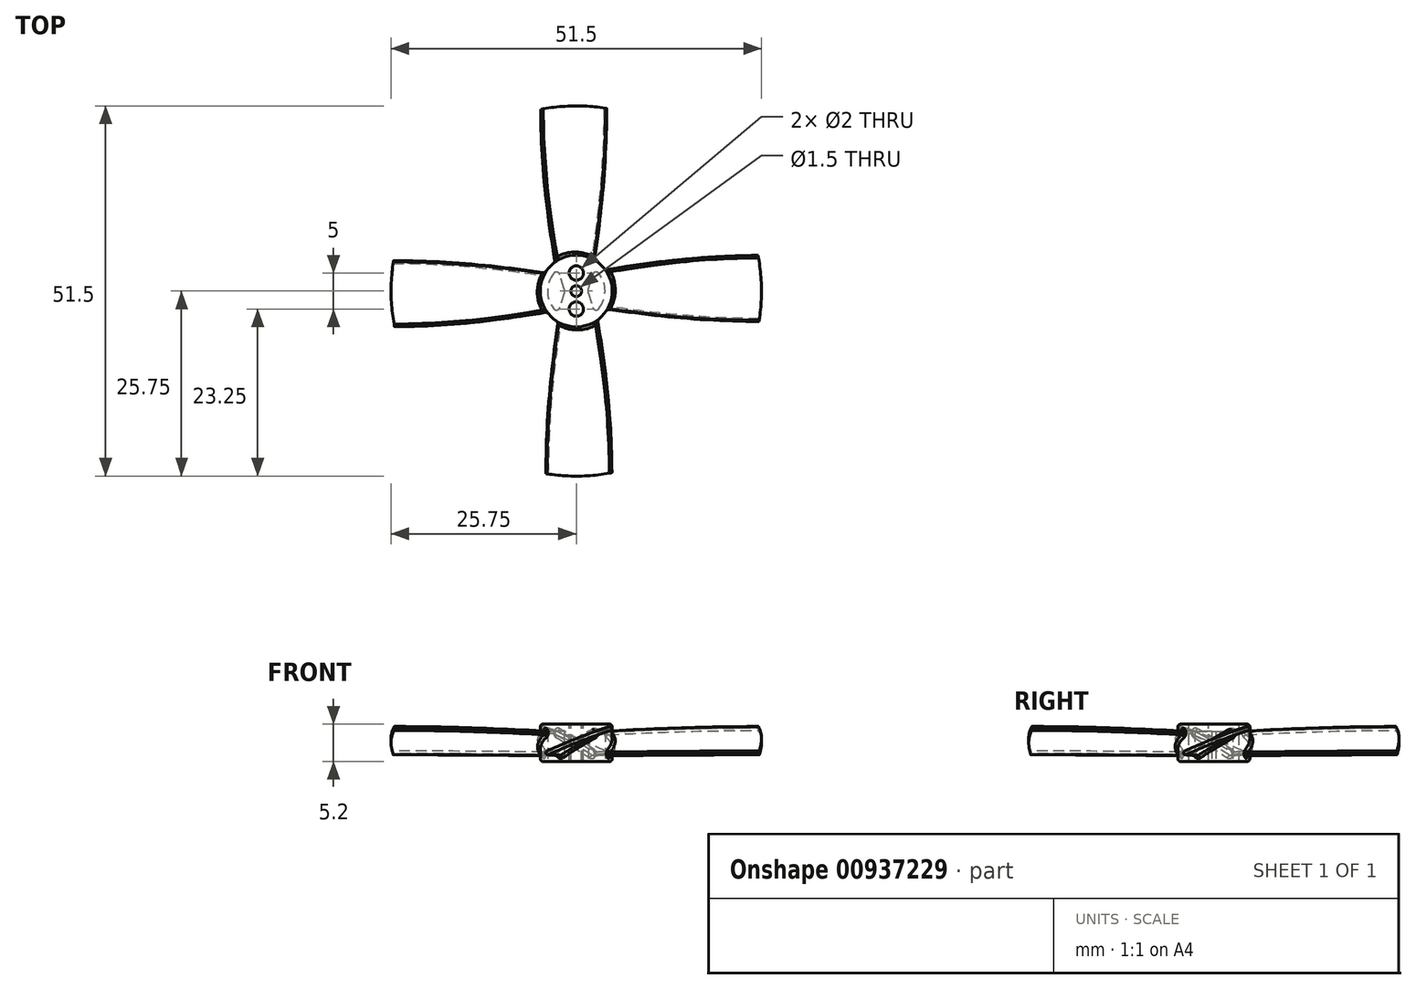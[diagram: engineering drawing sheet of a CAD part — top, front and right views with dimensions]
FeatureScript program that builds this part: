
annotation { "Feature Type Name" : "Feature", "Feature Type Description" : "" }
export const myFeature = defineFeature(function(context is Context, id is Id, definition is map)
    precondition{}
    {
        {
            var Q0;
            Q0=qCreatedBy(makeId("Top.planeOp"),FACE);
            var sketch = newSketch(context, id + "F0", { "sketchPlane" : qUnion([Q0])});
            skCircle(sketch, "E0", {"center": v(0, 0) * mm, "radius": 5 * mm});
            skPoint(sketch, "E1", {"position": v(0, 2.5) * mm});
            skPoint(sketch, "E2.MirrorP", {"position": v(0, -2.5) * mm});
            skSolve(sketch);
        }
        {
            var Q0;
            Q0=makeQuery(id+"F0.imprint","IMPRINT",FACE,{"disambiguationData":[TD([[makeQuery(id+"F0.imprint","IMPRINT",EDGE,{"derivedFrom":sQuery(id+"F0.wireOp",EDGE,"E0")}),1.0]])]});
            extrude(context, id + "F1", {"entities" : qUnion([Q0]), "oppositeDirection" : true, "depth" : 5.2 * mm, "offsetDistance" : 25 * mm});
        }
        {
            var Q0;
            Q0=qCreatedBy(makeId("Front.planeOp"),FACE);
            cPlane(context, id + "F2", {"entities" : qUnion([Q0]), "cplaneType" : CPlaneType.OFFSET, "offset" : (51.5 / 2) * mm, "width" : 150 * mm, "height" : 150 * mm});
        }
        {
            var Q0;
            Q0=qCreatedBy(id+"F2.planeOp",FACE);
            var sketch = newSketch(context, id + "F3", { "sketchPlane" : qUnion([Q0])});
            skArc(sketch, "E3", {"start": v(4.85, -0.26) * mm, "mid": v(0.22, -1.92) * mm, "end": v(-4.31, -3.85) * mm});
            skArc(sketch, "E4.0", {"start": v(5.02, -0.79) * mm, "mid": v(0.42, -2.43) * mm, "end": v(-4.08, -4.35) * mm});
            skLineSegment(sketch, "E5", {"start": v(30.5, -79.2) * mm, "end": v(-4.31, -3.85) * mm});
            skLineSegment(sketch, "E6", {"start": v(30.5, -79.2) * mm, "end": v(4.85, -0.26) * mm});
            skSolve(sketch);
        }
        {
            var Q0;
            Q0=qCreatedBy(makeId("Front.planeOp"),FACE);
            var sketch = newSketch(context, id + "F4", { "sketchPlane" : qUnion([Q0])});
            skArc(sketch, "E7", {"start": v(2.06, -1.11) * mm, "mid": v(0, -2.58) * mm, "end": v(-2.01, -4.11) * mm});
            skArc(sketch, "E8.0", {"start": v(2.37, -1.56) * mm, "mid": v(0.33, -3.02) * mm, "end": v(-1.67, -4.54) * mm});
            skLineSegment(sketch, "E9", {"start": v(48.93, -69) * mm, "end": v(-2.01, -4.11) * mm});
            skLineSegment(sketch, "E10", {"start": v(48.93, -69) * mm, "end": v(2.06, -1.11) * mm});
            skPoint(sketch, "E11", {"position": v(0, -2.58) * mm});
            skSolve(sketch);
        }
        {
            var Q0;
            {var subQ0=sQuery(id+"F4.wireOp",EDGE,"E7");Q0=makeQuery(id+"F4.imprint","IMPRINT",FACE,{"disambiguationData":[TD([[makeQuery(id+"F4.imprint","IMPRINT",EDGE,{"derivedFrom":subQ0}),1.0]])]});}
            var Q1;
            {var subQ0=sQuery(id+"F3.wireOp",EDGE,"E3");Q1=makeQuery(id+"F3.imprint","IMPRINT",FACE,{"disambiguationData":[TD([[makeQuery(id+"F3.imprint","IMPRINT",EDGE,{"derivedFrom":subQ0}),1.0]])]});}
            loft(context, id + "F5", {"startCondition" : LoftEndDerivativeType.TANGENT_TO_PROFILE, "startMagnitude" : 0, "endCondition" : LoftEndDerivativeType.NORMAL_TO_PROFILE, "endMagnitude" : 1.2, "sheetProfilesArray" : [{ "sheetProfileEntities" : qUnion([Q0]) }, { "sheetProfileEntities" : qUnion([Q1]) }]});
        }
        {
            var Q0;
            Q0=makeQuery(id+"F5.opLoft","SWEPT_EDGE",EDGE,{"disambiguationData":[OSD([sQuery(id+"F3.wireOp",EDGE,"E3"),sQuery(id+"F3.wireOp",EDGE,"E6"),sQuery(id+"F4.wireOp",EDGE,"E7"),sQuery(id+"F4.wireOp",EDGE,"E10")])]});
            var Q1;
            Q1=makeQuery(id+"F5.opLoft","SWEPT_EDGE",EDGE,{"disambiguationData":[OSD([sQuery(id+"F3.wireOp",EDGE,"E4.0"),sQuery(id+"F3.wireOp",EDGE,"E6"),sQuery(id+"F4.wireOp",EDGE,"E8.0"),sQuery(id+"F4.wireOp",EDGE,"E10")])]});
            var Q2;
            Q2=makeQuery(id+"F5.opLoft","SWEPT_EDGE",EDGE,{"disambiguationData":[OSD([sQuery(id+"F3.wireOp",EDGE,"E3"),sQuery(id+"F3.wireOp",EDGE,"E5"),sQuery(id+"F4.wireOp",EDGE,"E7"),sQuery(id+"F4.wireOp",EDGE,"E9")])]});
            var Q3;
            Q3=makeQuery(id+"F5.opLoft","SWEPT_EDGE",EDGE,{"disambiguationData":[OSD([sQuery(id+"F3.wireOp",EDGE,"E4.0"),sQuery(id+"F3.wireOp",EDGE,"E5"),sQuery(id+"F4.wireOp",EDGE,"E8.0"),sQuery(id+"F4.wireOp",EDGE,"E9")])]});
            fillet(context, id + "F6", {"entities" : qUnion([Q0, Q1, Q2, Q3]), "radius" : 0.27 * mm, "tangentPropagation" : true, "allowEdgeOverflow" : false});
        }
        {
            var Q0;
            Q0=qCreatedBy(makeId("Top.planeOp"),FACE);
            var sketch = newSketch(context, id + "F7", { "sketchPlane" : qUnion([Q0])});
            skCircle(sketch, "E12", {"center": v(0, 0) * mm, "radius": 25.75 * mm});
            skLineSegment(sketch, "E13.bottom", {"start": v(-26.5, 26.5) * mm, "end": v(26.5, 26.5) * mm});
            skLineSegment(sketch, "E13.top", {"start": v(-26.5, -26.5) * mm, "end": v(26.5, -26.5) * mm});
            skLineSegment(sketch, "E13.left", {"start": v(-26.5, 26.5) * mm, "end": v(-26.5, -26.5) * mm});
            skLineSegment(sketch, "E13.right", {"start": v(26.5, 26.5) * mm, "end": v(26.5, -26.5) * mm});
            skSolve(sketch);
        }
        {
            var Q0;
            Q0=makeQuery(id+"F7.imprint","IMPRINT",FACE,{"disambiguationData":[TD([[makeQuery(id+"F7.imprint","IMPRINT",EDGE,{"derivedFrom":sQuery(id+"F7.wireOp",EDGE,"E12")}),-1.0]])]});
            extrude(context, id + "F8", {"entities" : qUnion([Q0]), "operationType" : NewBodyOperationType.REMOVE, "oppositeDirection" : true, "depth" : 25 * mm, "offsetDistance" : 25 * mm});
        }
        {
            var Q0;
            {var subQ0=sQuery(id+"F4.wireOp",EDGE,"E7");var subQ4=sQuery(id+"F3.wireOp",EDGE,"E3");Q0=makeQuery(id+"F5.opLoft","SWEPT_BODY",BODY,{"disambiguationData":[OSD([makeQuery(id+"F3.imprint","IMPRINT",FACE,{"disambiguationData":[TD([[makeQuery(id+"F3.imprint","IMPRINT",EDGE,{"derivedFrom":subQ4}),1.0]])]}),makeQuery(id+"F4.imprint","IMPRINT",FACE,{"disambiguationData":[TD([[makeQuery(id+"F4.imprint","IMPRINT",EDGE,{"derivedFrom":subQ0}),1.0]])]})])]});}
            var Q1;
            Q1=sQuery(id+"F0.wireOp",EDGE,"E0");
            circularPattern(context, id + "F9", {"operationType" : NewBodyOperationType.ADD, "entities" : qUnion([Q0]), "axis" : qUnion([Q1]), "angle" : 360 * degree, "instanceCount" : 4, "equalSpace" : true});
        }
        {
            var Q0;
            Q0=sQuery(id+"F0.wireOp",VERTEX,"E1");
            var Q1;
            Q1=sQuery(id+"F0.wireOp",VERTEX,"E2.MirrorP");
            var Q2;
            Q2=makeQuery(id+"F1.opExtrude","SWEPT_BODY",BODY,{"disambiguationData":[OSD([sQuery(id+"F0.wireOp",EDGE,"E0")])]});
            hole(context, id + "F10", {"style" : HoleStyle.SIMPLE, "endStyle" : HoleEndStyle.THROUGH, "holeDiameter" : 2 * mm, "majorDiameter" : 5 * mm, "isTappedThrough" : true, "tappedDepth" : 12 * mm, "tapClearance" : 3, "locations" : qUnion([Q0, Q1]), "scope" : qUnion([Q2])});
        }
        {
            var Q0;
            Q0=sQuery(id+"F0.wireOp",VERTEX,"E0.center");
            var Q1;
            Q1=makeQuery(id+"F1.opExtrude","SWEPT_BODY",BODY,{"disambiguationData":[OSD([sQuery(id+"F0.wireOp",EDGE,"E0")])]});
            hole(context, id + "F11", {"style" : HoleStyle.SIMPLE, "endStyle" : HoleEndStyle.THROUGH, "holeDiameter" : 1.5 * mm, "majorDiameter" : 5 * mm, "isTappedThrough" : true, "tappedDepth" : 12 * mm, "tapClearance" : 3, "locations" : qUnion([Q0]), "scope" : qUnion([Q1])});
        }
        {
            var Q0;
            Q0=makeQuery(id+"F9.boolean.opBoolean","INTERSECT",EDGE,{"derivedFrom":[makeQuery(id+"F1.opExtrude","SWEPT_FACE",FACE,{"disambiguationData":[OSD([sQuery(id+"F0.wireOp",EDGE,"E0")])]}),makeQuery(id+"F5.opLoft","SWEPT_FACE",FACE,{"disambiguationData":[OSD([sQuery(id+"F3.wireOp",EDGE,"E3"),sQuery(id+"F3.wireOp",EDGE,"E5"),sQuery(id+"F3.wireOp",EDGE,"E6"),sQuery(id+"F4.wireOp",EDGE,"E7"),sQuery(id+"F4.wireOp",EDGE,"E9"),sQuery(id+"F4.wireOp",EDGE,"E10")])]})]});
            var Q1;
            Q1=makeQuery(id+"F9.boolean.opBoolean","INTERSECT",EDGE,{"derivedFrom":[makeQuery(id+"F1.opExtrude","SWEPT_FACE",FACE,{"disambiguationData":[OSD([sQuery(id+"F0.wireOp",EDGE,"E0")])]}),makeQuery(id+"F5.opLoft","SWEPT_FACE",FACE,{"disambiguationData":[OSD([sQuery(id+"F3.wireOp",EDGE,"E4.0"),sQuery(id+"F3.wireOp",EDGE,"E5"),sQuery(id+"F3.wireOp",EDGE,"E6"),sQuery(id+"F4.wireOp",EDGE,"E8.0"),sQuery(id+"F4.wireOp",EDGE,"E9"),sQuery(id+"F4.wireOp",EDGE,"E10")])]})]});
            var Q2;
            Q2=makeQuery(id+"F9.boolean.opBoolean","INTERSECT",EDGE,{"derivedFrom":[makeQuery(id+"F1.opExtrude","SWEPT_FACE",FACE,{"disambiguationData":[OSD([sQuery(id+"F0.wireOp",EDGE,"E0")])]}),makeQuery(id+"F5.opLoft","SWEPT_FACE",FACE,{"disambiguationData":[OSD([sQuery(id+"F3.wireOp",EDGE,"E3"),sQuery(id+"F3.wireOp",EDGE,"E4.0"),sQuery(id+"F3.wireOp",EDGE,"E5"),sQuery(id+"F4.wireOp",EDGE,"E7"),sQuery(id+"F4.wireOp",EDGE,"E8.0"),sQuery(id+"F4.wireOp",EDGE,"E9")])]})]});
            var Q3;
            Q3=makeQuery(id+"F9.boolean.opBoolean","INTERSECT",EDGE,{"derivedFrom":[makeQuery(id+"F1.opExtrude","SWEPT_FACE",FACE,{"disambiguationData":[OSD([sQuery(id+"F0.wireOp",EDGE,"E0")])]}),makeQuery(id+"F5.opLoft","SWEPT_FACE",FACE,{"disambiguationData":[OSD([sQuery(id+"F3.wireOp",EDGE,"E3"),sQuery(id+"F3.wireOp",EDGE,"E4.0"),sQuery(id+"F3.wireOp",EDGE,"E6"),sQuery(id+"F4.wireOp",EDGE,"E7"),sQuery(id+"F4.wireOp",EDGE,"E8.0"),sQuery(id+"F4.wireOp",EDGE,"E10")])]})]});
            var Q4;
            Q4=makeQuery(id+"F9.boolean.opBoolean","INTERSECT",EDGE,{"derivedFrom":[makeQuery(id+"F1.opExtrude","SWEPT_FACE",FACE,{"disambiguationData":[OSD([sQuery(id+"F0.wireOp",EDGE,"E0")])]}),makeQuery(id+"F9.opPattern","COPY",FACE,{"derivedFrom":makeQuery(id+"F5.opLoft","SWEPT_FACE",FACE,{"disambiguationData":[OSD([sQuery(id+"F3.wireOp",EDGE,"E3"),sQuery(id+"F3.wireOp",EDGE,"E5"),sQuery(id+"F3.wireOp",EDGE,"E6"),sQuery(id+"F4.wireOp",EDGE,"E7"),sQuery(id+"F4.wireOp",EDGE,"E9"),sQuery(id+"F4.wireOp",EDGE,"E10")])]}),"instanceName":"1"})]});
            var Q5;
            Q5=makeQuery(id+"F9.boolean.opBoolean","INTERSECT",EDGE,{"derivedFrom":[makeQuery(id+"F1.opExtrude","SWEPT_FACE",FACE,{"disambiguationData":[OSD([sQuery(id+"F0.wireOp",EDGE,"E0")])]}),makeQuery(id+"F9.opPattern","COPY",FACE,{"derivedFrom":makeQuery(id+"F5.opLoft","SWEPT_FACE",FACE,{"disambiguationData":[OSD([sQuery(id+"F3.wireOp",EDGE,"E3"),sQuery(id+"F3.wireOp",EDGE,"E4.0"),sQuery(id+"F3.wireOp",EDGE,"E5"),sQuery(id+"F4.wireOp",EDGE,"E7"),sQuery(id+"F4.wireOp",EDGE,"E8.0"),sQuery(id+"F4.wireOp",EDGE,"E9")])]}),"instanceName":"1"})]});
            var Q6;
            Q6=makeQuery(id+"F9.boolean.opBoolean","INTERSECT",EDGE,{"derivedFrom":[makeQuery(id+"F1.opExtrude","SWEPT_FACE",FACE,{"disambiguationData":[OSD([sQuery(id+"F0.wireOp",EDGE,"E0")])]}),makeQuery(id+"F9.opPattern","COPY",FACE,{"derivedFrom":makeQuery(id+"F5.opLoft","SWEPT_FACE",FACE,{"disambiguationData":[OSD([sQuery(id+"F3.wireOp",EDGE,"E4.0"),sQuery(id+"F3.wireOp",EDGE,"E5"),sQuery(id+"F3.wireOp",EDGE,"E6"),sQuery(id+"F4.wireOp",EDGE,"E8.0"),sQuery(id+"F4.wireOp",EDGE,"E9"),sQuery(id+"F4.wireOp",EDGE,"E10")])]}),"instanceName":"1"})]});
            var Q7;
            Q7=makeQuery(id+"F9.boolean.opBoolean","INTERSECT",EDGE,{"derivedFrom":[makeQuery(id+"F1.opExtrude","SWEPT_FACE",FACE,{"disambiguationData":[OSD([sQuery(id+"F0.wireOp",EDGE,"E0")])]}),makeQuery(id+"F9.opPattern","COPY",FACE,{"derivedFrom":makeQuery(id+"F5.opLoft","SWEPT_FACE",FACE,{"disambiguationData":[OSD([sQuery(id+"F3.wireOp",EDGE,"E3"),sQuery(id+"F3.wireOp",EDGE,"E4.0"),sQuery(id+"F3.wireOp",EDGE,"E6"),sQuery(id+"F4.wireOp",EDGE,"E7"),sQuery(id+"F4.wireOp",EDGE,"E8.0"),sQuery(id+"F4.wireOp",EDGE,"E10")])]}),"instanceName":"1"})]});
            var Q8;
            Q8=makeQuery(id+"F9.boolean.opBoolean","INTERSECT",EDGE,{"derivedFrom":[makeQuery(id+"F1.opExtrude","SWEPT_FACE",FACE,{"disambiguationData":[OSD([sQuery(id+"F0.wireOp",EDGE,"E0")])]}),makeQuery(id+"F9.opPattern","COPY",FACE,{"derivedFrom":makeQuery(id+"F5.opLoft","SWEPT_FACE",FACE,{"disambiguationData":[OSD([sQuery(id+"F3.wireOp",EDGE,"E3"),sQuery(id+"F3.wireOp",EDGE,"E4.0"),sQuery(id+"F3.wireOp",EDGE,"E5"),sQuery(id+"F4.wireOp",EDGE,"E7"),sQuery(id+"F4.wireOp",EDGE,"E8.0"),sQuery(id+"F4.wireOp",EDGE,"E9")])]}),"instanceName":"2"})]});
            var Q9;
            Q9=makeQuery(id+"F9.boolean.opBoolean","INTERSECT",EDGE,{"derivedFrom":[makeQuery(id+"F1.opExtrude","SWEPT_FACE",FACE,{"disambiguationData":[OSD([sQuery(id+"F0.wireOp",EDGE,"E0")])]}),makeQuery(id+"F9.opPattern","COPY",FACE,{"derivedFrom":makeQuery(id+"F5.opLoft","SWEPT_FACE",FACE,{"disambiguationData":[OSD([sQuery(id+"F3.wireOp",EDGE,"E3"),sQuery(id+"F3.wireOp",EDGE,"E5"),sQuery(id+"F3.wireOp",EDGE,"E6"),sQuery(id+"F4.wireOp",EDGE,"E7"),sQuery(id+"F4.wireOp",EDGE,"E9"),sQuery(id+"F4.wireOp",EDGE,"E10")])]}),"instanceName":"2"})]});
            var Q10;
            Q10=makeQuery(id+"F9.boolean.opBoolean","INTERSECT",EDGE,{"derivedFrom":[makeQuery(id+"F1.opExtrude","SWEPT_FACE",FACE,{"disambiguationData":[OSD([sQuery(id+"F0.wireOp",EDGE,"E0")])]}),makeQuery(id+"F9.opPattern","COPY",FACE,{"derivedFrom":makeQuery(id+"F5.opLoft","SWEPT_FACE",FACE,{"disambiguationData":[OSD([sQuery(id+"F3.wireOp",EDGE,"E4.0"),sQuery(id+"F3.wireOp",EDGE,"E5"),sQuery(id+"F3.wireOp",EDGE,"E6"),sQuery(id+"F4.wireOp",EDGE,"E8.0"),sQuery(id+"F4.wireOp",EDGE,"E9"),sQuery(id+"F4.wireOp",EDGE,"E10")])]}),"instanceName":"2"})]});
            var Q11;
            Q11=makeQuery(id+"F9.boolean.opBoolean","INTERSECT",EDGE,{"derivedFrom":[makeQuery(id+"F1.opExtrude","SWEPT_FACE",FACE,{"disambiguationData":[OSD([sQuery(id+"F0.wireOp",EDGE,"E0")])]}),makeQuery(id+"F9.opPattern","COPY",FACE,{"derivedFrom":makeQuery(id+"F5.opLoft","SWEPT_FACE",FACE,{"disambiguationData":[OSD([sQuery(id+"F3.wireOp",EDGE,"E3"),sQuery(id+"F3.wireOp",EDGE,"E4.0"),sQuery(id+"F3.wireOp",EDGE,"E6"),sQuery(id+"F4.wireOp",EDGE,"E7"),sQuery(id+"F4.wireOp",EDGE,"E8.0"),sQuery(id+"F4.wireOp",EDGE,"E10")])]}),"instanceName":"2"})]});
            var Q12;
            Q12=makeQuery(id+"F9.boolean.opBoolean","INTERSECT",EDGE,{"derivedFrom":[makeQuery(id+"F1.opExtrude","SWEPT_FACE",FACE,{"disambiguationData":[OSD([sQuery(id+"F0.wireOp",EDGE,"E0")])]}),makeQuery(id+"F9.opPattern","COPY",FACE,{"derivedFrom":makeQuery(id+"F5.opLoft","SWEPT_FACE",FACE,{"disambiguationData":[OSD([sQuery(id+"F3.wireOp",EDGE,"E3"),sQuery(id+"F3.wireOp",EDGE,"E4.0"),sQuery(id+"F3.wireOp",EDGE,"E5"),sQuery(id+"F4.wireOp",EDGE,"E7"),sQuery(id+"F4.wireOp",EDGE,"E8.0"),sQuery(id+"F4.wireOp",EDGE,"E9")])]}),"instanceName":"3"})]});
            var Q13;
            Q13=makeQuery(id+"F9.boolean.opBoolean","INTERSECT",EDGE,{"derivedFrom":[makeQuery(id+"F1.opExtrude","SWEPT_FACE",FACE,{"disambiguationData":[OSD([sQuery(id+"F0.wireOp",EDGE,"E0")])]}),makeQuery(id+"F9.opPattern","COPY",FACE,{"derivedFrom":makeQuery(id+"F5.opLoft","SWEPT_FACE",FACE,{"disambiguationData":[OSD([sQuery(id+"F3.wireOp",EDGE,"E3"),sQuery(id+"F3.wireOp",EDGE,"E5"),sQuery(id+"F3.wireOp",EDGE,"E6"),sQuery(id+"F4.wireOp",EDGE,"E7"),sQuery(id+"F4.wireOp",EDGE,"E9"),sQuery(id+"F4.wireOp",EDGE,"E10")])]}),"instanceName":"3"})]});
            var Q14;
            Q14=makeQuery(id+"F9.boolean.opBoolean","INTERSECT",EDGE,{"derivedFrom":[makeQuery(id+"F1.opExtrude","SWEPT_FACE",FACE,{"disambiguationData":[OSD([sQuery(id+"F0.wireOp",EDGE,"E0")])]}),makeQuery(id+"F9.opPattern","COPY",FACE,{"derivedFrom":makeQuery(id+"F5.opLoft","SWEPT_FACE",FACE,{"disambiguationData":[OSD([sQuery(id+"F3.wireOp",EDGE,"E4.0"),sQuery(id+"F3.wireOp",EDGE,"E5"),sQuery(id+"F3.wireOp",EDGE,"E6"),sQuery(id+"F4.wireOp",EDGE,"E8.0"),sQuery(id+"F4.wireOp",EDGE,"E9"),sQuery(id+"F4.wireOp",EDGE,"E10")])]}),"instanceName":"3"})]});
            var Q15;
            Q15=makeQuery(id+"F9.boolean.opBoolean","INTERSECT",EDGE,{"derivedFrom":[makeQuery(id+"F1.opExtrude","SWEPT_FACE",FACE,{"disambiguationData":[OSD([sQuery(id+"F0.wireOp",EDGE,"E0")])]}),makeQuery(id+"F9.opPattern","COPY",FACE,{"derivedFrom":makeQuery(id+"F5.opLoft","SWEPT_FACE",FACE,{"disambiguationData":[OSD([sQuery(id+"F3.wireOp",EDGE,"E3"),sQuery(id+"F3.wireOp",EDGE,"E4.0"),sQuery(id+"F3.wireOp",EDGE,"E6"),sQuery(id+"F4.wireOp",EDGE,"E7"),sQuery(id+"F4.wireOp",EDGE,"E8.0"),sQuery(id+"F4.wireOp",EDGE,"E10")])]}),"instanceName":"3"})]});
            fillet(context, id + "F12", {"entities" : qUnion([Q0, Q1, Q2, Q3, Q4, Q5, Q6, Q7, Q8, Q9, Q10, Q11, Q12, Q13, Q14, Q15]), "radius" : 0.4 * mm, "tangentPropagation" : true, "allowEdgeOverflow" : false});
        }
        {
            var Q0;
            Q0=makeQuery(id+"F1.opExtrude","CAP_FACE",FACE,{"disambiguationData":[OSD([sQuery(id+"F0.wireOp",EDGE,"E0")])],"isStart":false});
            var sketch = newSketch(context, id + "F13", { "sketchPlane" : qUnion([Q0])});
            skCircle(sketch, "E14", {"center": v(0, 0) * mm, "radius": 4 * mm});
            skCircle(sketch, "E15", {"center": v(0, 0) * mm, "radius": 1.7 * mm});
            skLineSegment(sketch, "E16", {"start": v(-1.68, 0.28) * mm, "end": v(-2.54, 3.1) * mm});
            skLineSegment(sketch, "E17.MirrorCS", {"start": v(-1.68, -0.28) * mm, "end": v(-2.54, -3.1) * mm});
            skLineSegment(sketch, "E18.MirrorCS", {"start": v(1.68, 0.28) * mm, "end": v(2.54, 3.1) * mm});
            skLineSegment(sketch, "E19.MirrorCS", {"start": v(1.68, -0.28) * mm, "end": v(2.54, -3.1) * mm});
            skSolve(sketch);
        }
        {
            var Q0;
            {var subQ0=sQuery(id+"F13.wireOp",EDGE,"E16");Q0=makeQuery(id+"F13.imprint","IMPRINT",FACE,{"disambiguationData":[TD([[makeQuery(id+"F13.imprint","IMPRINT",EDGE,{"derivedFrom":subQ0}),1.0]])]});}
            var Q1;
            {var subQ0=sQuery(id+"F13.wireOp",EDGE,"E18.MirrorCS");Q1=makeQuery(id+"F13.imprint","IMPRINT",FACE,{"disambiguationData":[TD([[makeQuery(id+"F13.imprint","IMPRINT",EDGE,{"derivedFrom":subQ0}),-1.0]])]});}
            var Q2;
            Q2=makeQuery(id+"F1.opExtrude","CAP_FACE",FACE,{"disambiguationData":[OSD([sQuery(id+"F0.wireOp",EDGE,"E0")])],"isStart":true});
            extrude(context, id + "F14", {"entities" : qUnion([Q0, Q1]), "operationType" : NewBodyOperationType.REMOVE, "endBound" : BoundingType.UP_TO_SURFACE, "oppositeDirection" : true, "depth" : 25 * mm, "endBoundEntityFace" : qUnion([Q2]), "hasOffset" : true, "offsetDistance" : 1 * mm});
        }
        {
            var Q0;
            Q0=makeQuery(id+"F14.boolean.opBoolean","COPY",EDGE,{"derivedFrom":makeQuery(id+"F14.opExtrude","SWEPT_EDGE",EDGE,{"disambiguationData":[OSD([sQuery(id+"F13.wireOp",EDGE,"E14"),sQuery(id+"F13.wireOp",EDGE,"E16")])]})});
            var Q1;
            Q1=makeQuery(id+"F14.boolean.opBoolean","COPY",EDGE,{"derivedFrom":makeQuery(id+"F14.opExtrude","SWEPT_EDGE",EDGE,{"disambiguationData":[OSD([sQuery(id+"F13.wireOp",EDGE,"E14"),sQuery(id+"F13.wireOp",EDGE,"E18.MirrorCS")])]})});
            var Q2;
            Q2=makeQuery(id+"F14.boolean.opBoolean","COPY",EDGE,{"derivedFrom":makeQuery(id+"F14.opExtrude","SWEPT_EDGE",EDGE,{"disambiguationData":[OSD([sQuery(id+"F13.wireOp",EDGE,"E14"),sQuery(id+"F13.wireOp",EDGE,"E19.MirrorCS")])]})});
            var Q3;
            Q3=makeQuery(id+"F14.boolean.opBoolean","COPY",EDGE,{"derivedFrom":makeQuery(id+"F14.opExtrude","SWEPT_EDGE",EDGE,{"disambiguationData":[OSD([sQuery(id+"F13.wireOp",EDGE,"E14"),sQuery(id+"F13.wireOp",EDGE,"E17.MirrorCS")])]})});
            fillet(context, id + "F15", {"entities" : qUnion([Q0, Q1, Q2, Q3]), "radius" : 0.5 * mm, "tangentPropagation" : true, "allowEdgeOverflow" : false});
        }
        {
            var Q0;
            Q0=makeQuery(id+"F1.opExtrude","CAP_EDGE",EDGE,{"disambiguationData":[OSD([sQuery(id+"F0.wireOp",EDGE,"E0")])],"isStart":true});
            var Q1;
            Q1=makeQuery(id+"F1.opExtrude","CAP_EDGE",EDGE,{"disambiguationData":[OSD([sQuery(id+"F0.wireOp",EDGE,"E0")])],"isStart":false});
            fillet(context, id + "F16", {"entities" : qUnion([Q0, Q1]), "radius" : 0.4 * mm, "tangentPropagation" : true, "allowEdgeOverflow" : false});
        }
    });
